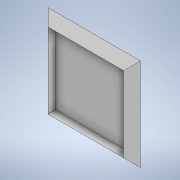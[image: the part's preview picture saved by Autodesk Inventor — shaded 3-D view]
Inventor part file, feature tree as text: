
AUTODESK INVENTOR PART (.ipt)
format: ipt  version: 2021 (Build 250183000, 183)  size: 106,496 bytes
history: native  units: in
note: dims shown in document units (in); Inventor stores cm internally (conversion verified against a paired STEP export)
features: extrude x2, sketch x2, chamfer x1, projected_geometry x1
ambient origin geometry x8: Origin, YZ Plane, XZ Plane, XY Plane, X Axis, Y Axis, Z Axis, Center Point
bodies: Solid1 (feature_tree)
feature tree (6):
  extrude  "Extrusion1"  Depth=1.7323in
  chamfer  "Chamfer1"  Distance=0.1575in
  extrude  "Extrusion2"  Depth=0.1417in TaperAngle=0.0deg
  sketch  "Sketch1"  dims[d0=1.7323in d1=1.7323in d2=0.1575in d3=0.0in]
  sketch  "Sketch2"  dims[d4=0.1575in d5=0.0787in d6=45.0deg d7=0.1417in d8=0.0in]
  projected_geometry  "Projected Loop1"
